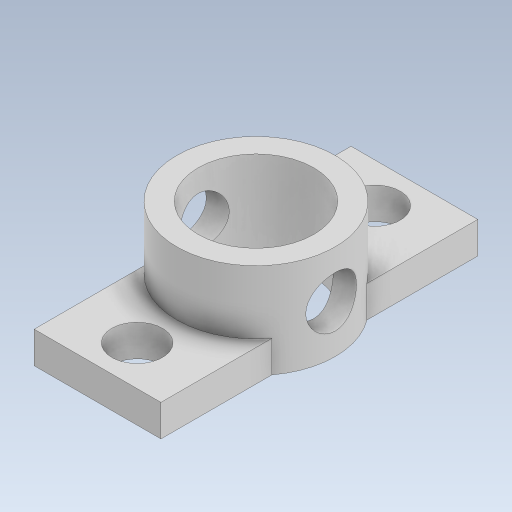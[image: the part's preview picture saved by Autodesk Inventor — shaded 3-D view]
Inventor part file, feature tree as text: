
AUTODESK INVENTOR PART (.ipt)
format: ipt  version: 2023.5 (Build 275446000, 446)  size: 158,720 bytes
history: native  units: mm
features: extrude x3, sketch x2, plane x1
ambient origin geometry x8: Origin, YZ Plane, XZ Plane, XY Plane, X Axis, Y Axis, Z Axis, Center Point
bodies: Solid1 (feature_tree)
feature tree (6):
  sketch  "Sketch1"  dims[d0=7.3mm d1=10.0mm]
  extrude  "Extrusion1"  Depth=10.0mm
  extrude  "Extrusion2"  Depth=10.0mm
  plane  "Work Plane1"
  extrude  "Extrusion3"  Depth=10.0mm
  sketch  "Sketch2"  dims[d2=20.0mm d3=3.2mm d4=2.5mm d5=3.2mm d6=2.5mm d7=2.0mm d8=0.0mm d9=6.0mm d10=0.0mm d11=3.2mm d12=10.0mm d13=0.0mm]
